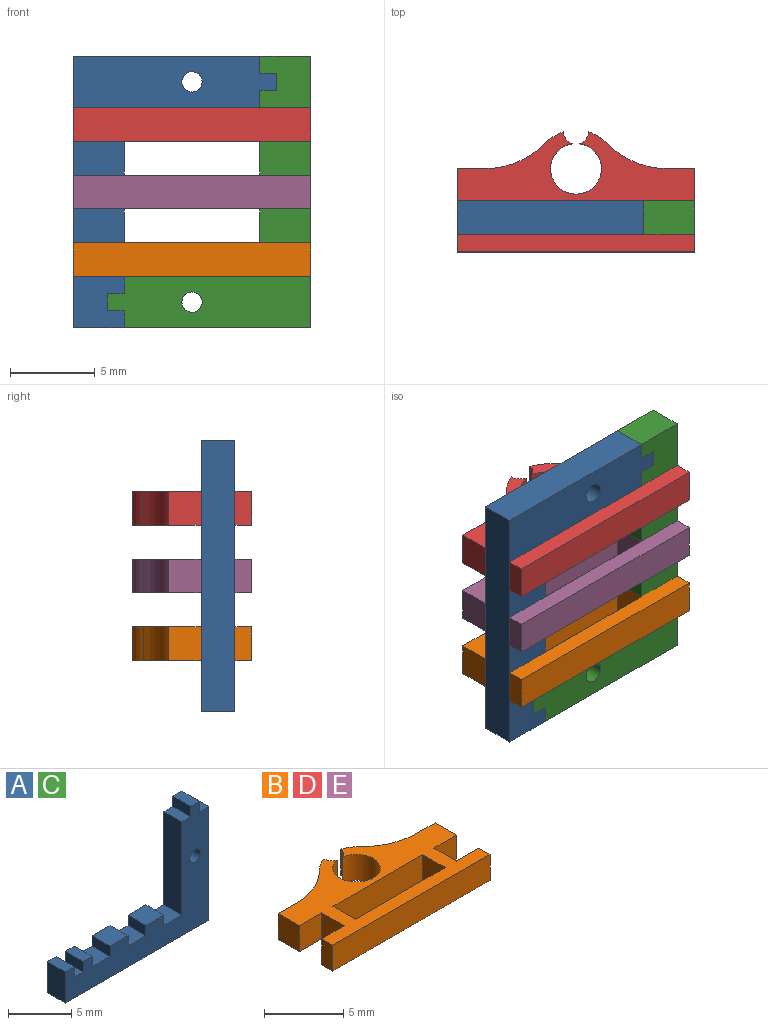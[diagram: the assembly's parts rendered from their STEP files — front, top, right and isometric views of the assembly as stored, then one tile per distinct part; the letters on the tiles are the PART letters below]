
ASSEMBLY  parts=5 mates=10
PART A: 27 faces, bbox 16x2x12 mm
  f0: plane 11x2mm, normal (1,0,0), area 22mm2, adj f1,f23,f25,f26
  f1: plane 2x1mm, normal (0,0,1), area 2mm2, adj f0,f2,f25,f26
  f2: plane 2x1mm, normal (1,0,0), area 2mm2, adj f1,f3,f25,f26
  f3: plane 2x1mm, normal (0,0,1), area 2mm2, adj f2,f4,f25,f26
  f4: plane 2x1mm, normal (-1,0,0), area 2mm2, adj f3,f5,f25,f26
  f5: plane 2x1mm, normal (0,0,1), area 2mm2, adj f4,f6,f25,f26
  f6: plane 9x2mm, normal (-1,0,0), area 18mm2, adj f5,f7,f25,f26
  f7: plane 2x2mm, normal (0,0,1), area 4mm2, adj f6,f8,f25,f26
  f8: plane 2x1mm, normal (1,0,0), area 2mm2, adj f7,f9,f25,f26
  f9: plane 2x2mm, normal (0,0,1), area 4mm2, adj f8,f10,f25,f26
  f10: plane 2x1mm, normal (-1,0,0), area 2mm2, adj f9,f11,f25,f26
  f11: plane 2x2mm, normal (0,0,1), area 4mm2, adj f10,f12,f25,f26
  f12: plane 2x1mm, normal (1,0,0), area 2mm2, adj f11,f13,f25,f26
  f13: plane 2x2mm, normal (0,0,1), area 4mm2, adj f12,f14,f25,f26
  f14: plane 2x1mm, normal (-1,0,0), area 2mm2, adj f13,f15,f25,f26
  f15: plane 2x2mm, normal (0,0,1), area 4mm2, adj f14,f16,f25,f26
  f16: plane 2x1mm, normal (1,0,0), area 2mm2, adj f15,f17,f25,f26
  f17: plane 2x1mm, normal (0,0,1), area 2mm2, adj f16,f18,f25,f26
  f18: plane 2x1mm, normal (-1,0,0), area 2mm2, adj f17,f19,f25,f26
  f19: plane 2x1mm, normal (0,0,1), area 2mm2, adj f18,f20,f25,f26
  f20: plane 2x1mm, normal (1,0,0), area 2mm2, adj f19,f21,f25,f26
  f21: plane 2x1mm, normal (0,0,1), area 2mm2, adj f20,f22,f25,f26
  f22: plane 3x2mm, normal (-1,0,0), area 6mm2, adj f21,f23,f25,f26
  f23: plane 16x2mm, normal (0,0,-1), area 32mm2, adj f0,f22,f25,f26
  f24: cylinder r=0.6mm len=2mm, axis (0,1,0), area 7.5mm2, adj f25,f26
  f25: plane 16x12mm, normal (0,-1,0), area 64.9mm2, adj f0,f1,f2,f3,f4,f5,f6,f7
  f26: plane 16x12mm, normal (0,1,0), area 64.9mm2, adj f0,f1,f2,f3,f4,f5,f6,f7
PART B: 26 faces, bbox 14x7.1x2 mm
  f0: plane 14x7.07mm, normal (0,0,1), area 47.3mm2, adj f2,f3,f4,f5,f6,f7,f8,f9
  f1: plane 14x7.07mm, normal (0,0,-1), area 47.3mm2, adj f2,f3,f4,f5,f6,f7,f8,f9
  f2: cylinder r=2.5mm len=2mm, axis (0,0,-1), area 2.5mm2, adj f0,f1,f5,f25
  f3: cylinder r=0.75mm len=2mm, axis (0,0,-1), area 1.8mm2, adj f0,f1,f4,f6
  f4: cylinder r=2.5mm len=2mm, axis (0,0,-1), area 2.5mm2, adj f0,f1,f3,f24
  f5: cylinder r=0.75mm len=2mm, axis (0,0,-1), area 1.8mm2, adj f0,f1,f2,f6
  f6: cylinder r=1.5mm len=3mm, axis (0,0,-1), area 18mm2, adj f0,f1,f3,f5
  f7: plane 2x1.61mm, normal (0,1,0), area 3.2mm2, adj f0,f1,f8,f24
  f8: plane 2x1.9mm, normal (-1,0,0), area 3.8mm2, adj f0,f1,f7,f9
  f9: plane 2x2mm, normal (0,-1,0), area 4mm2, adj f0,f1,f8,f10
  f10: plane 2x2mm, normal (-1,0,0), area 4mm2, adj f0,f1,f9,f11
  f11: plane 2x2mm, normal (0,1,0), area 4mm2, adj f0,f1,f10,f12
  f12: plane 2x1mm, normal (-1,0,0), area 2mm2, adj f0,f1,f11,f13
  f13: plane 14x2mm, normal (0,-1,0), area 28mm2, adj f0,f1,f12,f14
  f14: plane 2x1mm, normal (1,0,0), area 2mm2, adj f0,f1,f13,f15
  f15: plane 2x2mm, normal (0,1,0), area 4mm2, adj f0,f1,f14,f16
  f16: plane 2x2mm, normal (1,0,0), area 4mm2, adj f0,f1,f15,f17
  f17: plane 2x2mm, normal (0,-1,0), area 4mm2, adj f0,f1,f16,f18
  f18: plane 2x1.9mm, normal (1,0,0), area 3.8mm2, adj f0,f1,f17,f19
  f19: plane 2x1.61mm, normal (0,1,0), area 3.2mm2, adj f0,f1,f18,f25
  f20: plane 8x2mm, normal (0,-1,0), area 16mm2, adj f0,f1,f21,f23
  f21: plane 2x2mm, normal (-1,0,0), area 4mm2, adj f0,f1,f20,f22
  f22: plane 8x2mm, normal (0,1,0), area 16mm2, adj f0,f1,f21,f23
  f23: plane 2x2mm, normal (1,0,0), area 4mm2, adj f0,f1,f20,f22
  f24: cylinder r=5mm len=3.59mm, axis (0,0,-1), area 8mm2, adj f0,f1,f4,f7
  f25: cylinder r=5mm len=3.59mm, axis (0,0,-1), area 8mm2, adj f0,f1,f2,f19
PART C: same geometry as A
PART D: same geometry as B
PART E: same geometry as B
PLACE A rot(axis=(-0.71,0,-0.71),180deg) t=(-9.96,7.06,-6.28)mm
PLACE B t=(-3.96,10.96,-11.28)mm
PLACE C rot(axis=(0.71,0,-0.71),180deg) t=(2.04,7.06,-6.28)mm
PLACE D t=(-3.96,10.96,-3.28)mm
PLACE E t=(-3.96,10.96,-7.28)mm
MATE planar B.f1 <-> C.f6  axis (0,0,-1) through (-3.96,6.06,-11.28)mm
MATE planar D.f1 <-> A.f8  axis (0,0,-1) through (-3.96,9.04,-3.28)mm
MATE planar E.f18 <-> D.f18  axis (1,0,0) through (3.04,10.01,-6.28)mm
MATE planar E.f18 <-> B.f18  axis (1,0,0) through (3.04,10.01,-6.28)mm
MATE planar A.f22 <-> C.f0  axis (0,0,-1) through (-9.46,8.06,-14.28)mm
MATE planar C.f7 <-> D.f16  axis (-1,0,0) through (1.04,8.06,-10.28)mm
MATE planar D.f18 <-> E.f18  axis (1,0,0) through (3.04,10.01,-2.28)mm
MATE planar A.f7 <-> D.f10  axis (1,0,0) through (-8.96,8.06,-2.28)mm
MATE planar E.f15 <-> C.f26  axis (0,1,0) through (2.04,7.06,-6.28)mm
MATE planar E.f1 <-> A.f12  axis (0,0,-1) through (-3.96,9.04,-7.28)mm
